FCSTD DOCUMENT  (FreeCAD 0.20R29410 (Git))
Label: FanController
License: All rights reserved
LicenseURL: http://en.wikipedia.org/wiki/All_rights_reserved
objects: PartDesign::Body×2, Sketcher::SketchObject×1
note: 3 computed .brp shape members not serialized (recipe doc carries the construction recipe); baked Part::Feature solids carry a one-line shape summary decoded from their .brp

FEATURE [Sketcher::SketchObject] Sketch  label="bottom001"
  FullyConstrained = true
  MapMode = 5
  Support = -> [XY_Plane]
  sketch-geometry (78):
    g0: LineSegment StartX=-242.5 StartY=-23 StartZ=0 EndX=242.5 EndY=-23 EndZ=0
    g1: LineSegment StartX=242.5 StartY=23 StartZ=0 EndX=-242.5 EndY=23 EndZ=0
    g2: ArcOfCircle CenterX=-215.5 CenterY=16 CenterZ=0 NormalX=0 NormalY=0 NormalZ=1 AngleXU=0 Radius=3 StartAngle=4.71239 EndAngle=7.85398
    g3: LineSegment StartX=-242.5 StartY=19 StartZ=0 EndX=-215.5 EndY=19 EndZ=0
    g4: LineSegment StartX=-215.5 StartY=13 StartZ=0 EndX=-242.5 EndY=13 EndZ=0
    g5: ArcOfCircle CenterX=-215.5 CenterY=-2e-16 CenterZ=0 NormalX=0 NormalY=0 NormalZ=1 AngleXU=0 Radius=3 StartAngle=4.71239 EndAngle=7.85398
    g6: LineSegment StartX=-242.5 StartY=3 StartZ=0 EndX=-215.5 EndY=3 EndZ=0
    g7: LineSegment StartX=-215.5 StartY=-3 StartZ=0 EndX=-242.5 EndY=-3 EndZ=0
    g8: ArcOfCircle CenterX=-215.5 CenterY=-16 CenterZ=0 NormalX=0 NormalY=0 NormalZ=1 AngleXU=0 Radius=3 StartAngle=4.71239 EndAngle=7.85398
    g9: LineSegment StartX=-215.5 StartY=-13 StartZ=0 EndX=-242.5 EndY=-13 EndZ=0
    g10: LineSegment StartX=-215.5 StartY=-19 StartZ=0 EndX=-242.5 EndY=-19 EndZ=0
    g11: ArcOfCircle CenterX=215.5 CenterY=-16 CenterZ=0 NormalX=0 NormalY=0 NormalZ=1 AngleXU=0 Radius=3 StartAngle=1.5708 EndAngle=4.71239
    g12: ArcOfCircle CenterX=215.5 CenterY=2e-16 CenterZ=0 NormalX=0 NormalY=0 NormalZ=1 AngleXU=0 Radius=3 StartAngle=1.5708 EndAngle=4.71239
    g13: ArcOfCircle CenterX=215.5 CenterY=16 CenterZ=0 NormalX=0 NormalY=0 NormalZ=1 AngleXU=0 Radius=3 StartAngle=1.5708 EndAngle=4.71239
    g14: LineSegment StartX=215.5 StartY=19 StartZ=0 EndX=242.5 EndY=19 EndZ=0
    g15: LineSegment StartX=215.5 StartY=13 StartZ=0 EndX=242.5 EndY=13 EndZ=0
    g16: LineSegment StartX=215.5 StartY=3 StartZ=0 EndX=242.5 EndY=3 EndZ=0
    g17: LineSegment StartX=215.5 StartY=-3 StartZ=0 EndX=242.5 EndY=-3 EndZ=0
    g18: LineSegment StartX=215.5 StartY=-13 StartZ=0 EndX=242.5 EndY=-13 EndZ=0
    g19: LineSegment StartX=215.5 StartY=-19 StartZ=0 EndX=242.5 EndY=-19 EndZ=0
    g20: Circle CenterX=-145 CenterY=18 CenterZ=0 NormalX=0 NormalY=0 NormalZ=1 AngleXU=0 Radius=1.6
    g21: GeomPoint X=0 Y=23 Z=0
    g22: Circle CenterX=-145 CenterY=18 CenterZ=0 NormalX=0 NormalY=0 NormalZ=1 AngleXU=0 Radius=3
    g23: Circle CenterX=-145 CenterY=18 CenterZ=0 NormalX=0 NormalY=0 NormalZ=1 AngleXU=0 Radius=3.25
    g24: Circle CenterX=-145 CenterY=-18 CenterZ=0 NormalX=0 NormalY=0 NormalZ=1 AngleXU=0 Radius=1.6
    g25: Circle CenterX=-145 CenterY=-18 CenterZ=0 NormalX=0 NormalY=0 NormalZ=1 AngleXU=0 Radius=3
    g26: Circle CenterX=-145 CenterY=-18 CenterZ=0 NormalX=0 NormalY=0 NormalZ=1 AngleXU=0 Radius=3.25
    g27: Circle CenterX=145 CenterY=-18 CenterZ=0 NormalX=0 NormalY=0 NormalZ=1 AngleXU=0 Radius=1.6
    g28: Circle CenterX=145 CenterY=-18 CenterZ=0 NormalX=0 NormalY=0 NormalZ=1 AngleXU=0 Radius=3
    g29: Circle CenterX=145 CenterY=-18 CenterZ=0 NormalX=0 NormalY=0 NormalZ=1 AngleXU=0 Radius=3.25
    g30: Circle CenterX=145 CenterY=18 CenterZ=0 NormalX=0 NormalY=0 NormalZ=1 AngleXU=0 Radius=3.25
    g31: LineSegment StartX=-242.5 StartY=23 StartZ=0 EndX=-242.5 EndY=19 EndZ=0
    g32: LineSegment StartX=-242.5 StartY=13 StartZ=0 EndX=-242.5 EndY=3 EndZ=0
    g33: LineSegment StartX=-242.5 StartY=-3 StartZ=0 EndX=-242.5 EndY=-13 EndZ=0
    g34: LineSegment StartX=-242.5 StartY=-19 StartZ=0 EndX=-242.5 EndY=-23 EndZ=0
    g35: Circle CenterX=145 CenterY=18 CenterZ=0 NormalX=0 NormalY=0 NormalZ=1 AngleXU=0 Radius=1.6
    g36: Circle CenterX=145 CenterY=18 CenterZ=0 NormalX=0 NormalY=0 NormalZ=1 AngleXU=0 Radius=3
    g37: LineSegment StartX=242.5 StartY=23 StartZ=0 EndX=242.5 EndY=19 EndZ=0
    g38: LineSegment StartX=242.5 StartY=19 StartZ=0 EndX=242.5 EndY=13 EndZ=0
    g39: LineSegment StartX=242.5 StartY=13 StartZ=0 EndX=242.5 EndY=3 EndZ=0
    g40: LineSegment StartX=242.5 StartY=-3 StartZ=0 EndX=242.5 EndY=-13 EndZ=0
    g41: LineSegment StartX=242.5 StartY=-19 StartZ=0 EndX=242.5 EndY=-23 EndZ=0
    g42: Circle CenterX=34.3 CenterY=19.65 CenterZ=0 NormalX=0 NormalY=0 NormalZ=1 AngleXU=0 Radius=1.6
    g43: Circle CenterX=34.3 CenterY=19.65 CenterZ=0 NormalX=0 NormalY=0 NormalZ=1 AngleXU=0 Radius=3
    g44: Circle CenterX=34.3 CenterY=19.65 CenterZ=0 NormalX=0 NormalY=0 NormalZ=1 AngleXU=0 Radius=3.25
    g45: Circle CenterX=34.3 CenterY=-19.65 CenterZ=0 NormalX=0 NormalY=0 NormalZ=1 AngleXU=0 Radius=1.6
    g46: Circle CenterX=34.3 CenterY=-19.65 CenterZ=0 NormalX=0 NormalY=0 NormalZ=1 AngleXU=0 Radius=3
    g47: Circle CenterX=34.3 CenterY=-19.65 CenterZ=0 NormalX=0 NormalY=0 NormalZ=1 AngleXU=0 Radius=3.25
    g48: Circle CenterX=-34.3 CenterY=19.65 CenterZ=0 NormalX=0 NormalY=0 NormalZ=1 AngleXU=0 Radius=1.6
    g49: Circle CenterX=-34.3 CenterY=19.65 CenterZ=0 NormalX=0 NormalY=0 NormalZ=1 AngleXU=0 Radius=3
    g50: Circle CenterX=-34.3 CenterY=19.65 CenterZ=0 NormalX=0 NormalY=0 NormalZ=1 AngleXU=0 Radius=3.25
    g51: Circle CenterX=-34.3 CenterY=-19.65 CenterZ=0 NormalX=0 NormalY=0 NormalZ=1 AngleXU=0 Radius=1.6
    g52: Circle CenterX=-34.3 CenterY=-19.65 CenterZ=0 NormalX=0 NormalY=0 NormalZ=1 AngleXU=0 Radius=3
    g53: Circle CenterX=-34.3 CenterY=-19.65 CenterZ=0 NormalX=0 NormalY=0 NormalZ=1 AngleXU=0 Radius=3.25
    g54: LineSegment StartX=-150.5 StartY=-20.5 StartZ=0 EndX=-150.5 EndY=-18 EndZ=0
    g55: LineSegment StartX=-150.5 StartY=-15.5 StartZ=0 EndX=-150.5 EndY=-13 EndZ=0
    g56: LineSegment StartX=-152.5 StartY=-13 StartZ=0 EndX=-152.5 EndY=-15.5 EndZ=0
    g57: LineSegment StartX=-152.5 StartY=-20.5 StartZ=0 EndX=-152.5 EndY=-18 EndZ=0
    g58: LineSegment StartX=-152.5 StartY=-15.5 StartZ=0 EndX=-150.5 EndY=-15.5 EndZ=0
    g59: LineSegment StartX=-152.5 StartY=-13 StartZ=0 EndX=-150.5 EndY=-13 EndZ=0
    g60: LineSegment StartX=-152.5 StartY=-18 StartZ=0 EndX=-150.5 EndY=-18 EndZ=0
    g61: LineSegment StartX=-150.5 StartY=-20.5 StartZ=0 EndX=-152.5 EndY=-20.5 EndZ=0
    g62: LineSegment StartX=-150.5 StartY=20.5 StartZ=0 EndX=-150.5 EndY=18 EndZ=0
    g63: LineSegment StartX=-150.5 StartY=15.5 StartZ=0 EndX=-150.5 EndY=13 EndZ=0
    g64: LineSegment StartX=-152.5 StartY=20.5 StartZ=0 EndX=-152.5 EndY=18 EndZ=0
    g65: LineSegment StartX=-152.5 StartY=15.5 StartZ=0 EndX=-152.5 EndY=13 EndZ=0
    g66: LineSegment StartX=-152.5 StartY=20.5 StartZ=0 EndX=-150.5 EndY=20.5 EndZ=0
    g67: LineSegment StartX=-150.5 StartY=18 StartZ=0 EndX=-152.5 EndY=18 EndZ=0
    g68: LineSegment StartX=-152.5 StartY=15.5 StartZ=0 EndX=-150.5 EndY=15.5 EndZ=0
    g69: LineSegment StartX=-150.5 StartY=13 StartZ=0 EndX=-152.5 EndY=13 EndZ=0
    g70: LineSegment StartX=150.5 StartY=-15.5 StartZ=0 EndX=150.5 EndY=-20.5 EndZ=0
    g71: LineSegment StartX=152.5 StartY=-20.5 StartZ=0 EndX=152.5 EndY=-15.5 EndZ=0
    g72: LineSegment StartX=150.5 StartY=-20.5 StartZ=0 EndX=152.5 EndY=-20.5 EndZ=0
    g73: LineSegment StartX=152.5 StartY=-15.5 StartZ=0 EndX=150.5 EndY=-15.5 EndZ=0
    g74: LineSegment StartX=150.5 StartY=20.5 StartZ=0 EndX=150.5 EndY=15.5 EndZ=0
    g75: LineSegment StartX=152.5 StartY=20.5 StartZ=0 EndX=152.5 EndY=15.5 EndZ=0
    g76: LineSegment StartX=150.5 StartY=20.5 StartZ=0 EndX=152.5 EndY=20.5 EndZ=0
    g77: LineSegment StartX=150.5 StartY=15.5 StartZ=0 EndX=152.5 EndY=15.5 EndZ=0
  constraints (222):
    c: Horizontal(g0)
    c: Horizontal(g1)
    c: DistanceX(g1,g1) = 485
    c: DistanceY(g0,g1) = 46
    c: Diameter(g2) = 6
    c: Vertical(g2,g2)
    c: Vertical(g2,g2)
    c: Coincident(g3,g2)
    c: Coincident(g4,g2)
    c: Parallel(g3,g1)
    c: Parallel(g1,g4)
    c: Diameter(g5) = 6
    c: Vertical(g5,g5)
    c: Vertical(g5,g5)
    c: Coincident(g6,g5)
    c: Coincident(g7,g5)
    c: Diameter(g8) = 6
    c: Vertical(g8,g8)
    c: Vertical(g8,g8)
    c: Coincident(g9,g8)
    c: Horizontal(g9)
    c: Coincident(g10,g8)
    c: Horizontal(g10)
    c: Parallel(g1,g6)
    c: Parallel(g1,g7)
    c: Equal(g12,g13)
    c: Equal(g12,g11)
    c: Diameter(g12) = 6
    c: Vertical(g13,g13)
    c: Vertical(g13,g13)
    c: Vertical(g12,g12)
    c: Vertical(g12,g12)
    c: Vertical(g11,g11)
    c: Vertical(g11,g11)
    c: Vertical(g13,g12)
    c: Vertical(g12,g11)
    c: Coincident(g14,g13)
    c: Horizontal(g14)
    c: Coincident(g15,g13)
    c: Horizontal(g15)
    c: Coincident(g16,g12)
    c: Horizontal(g16)
    c: Coincident(g17,g12)
    c: Horizontal(g17)
    c: Coincident(g18,g11)
    c: Horizontal(g18)
    c: Coincident(g19,g11)
    c: Horizontal(g19)
    c: DistanceX(g13,g14) = 27
    c: Vertical(g2,g5)
    c: Vertical(g5,g8)
    c: Diameter(g20) = 3.2
    c: PointOnObject(g21,g1)
    c: PointOnObject(g21,g-2)
    c: Coincident(g22,g20)
    c: Diameter(g22) = 6
    c: Coincident(g23,g20)
    c: Diameter(g23) = 6.5
    c: Coincident(g25,g24)
    c: Coincident(g26,g24)
    c: Diameter(g24) = 3.2
    c: Diameter(g25) = 6
    c: Diameter(g26) = 6.5
    c: Coincident(g29,g28)
    c: Coincident(g27,g28)
    c: Diameter(g27) = 3.2
    c: Diameter(g28) = 6
    c: Diameter(g29) = 6.5
    c: Diameter(g30) = 6.5
    c: Vertical(g1,g14)
    c: Vertical(g14,g15)
    c: Vertical(g15,g16)
    c: Vertical(g16,g17)
    c: Vertical(g17,g18)
    c: Vertical(g18,g19)
    c: Vertical(g19,g0)
    c: Vertical(g3,g1)
    c: Vertical(g1,g4)
    c: Vertical(g4,g6)
    c: Vertical(g6,g7)
    c: Vertical(g7,g9)
    c: Vertical(g9,g10)
    c: Vertical(g10,g0)
    c: DistanceY(g-1,g21) = 23
    c: DistanceX(g1,g21) = 242.5
    c: Coincident(g31,g1)
    c: Coincident(g31,g3)
    c: Coincident(g32,g4)
    c: Coincident(g32,g6)
    c: Coincident(g33,g7)
    c: Coincident(g33,g9)
    c: Coincident(g34,g10)
    c: Coincident(g34,g0)
    c: Distance(g3,g1) = 4
    c: Distance(g4,g6) = 10
    c: Distance(g7,g9) = 10
    c: DistanceX(g3,g3) = 27
    c: Coincident(g35,g30)
    c: Coincident(g36,g30)
    c: Diameter(g35) = 3.2
    c: Diameter(g36) = 6
    c: Coincident(g37,g1)
    c: Coincident(g37,g14)
    c: Coincident(g38,g14)
    c: Coincident(g38,g15)
    c: Coincident(g39,g15)
    c: Coincident(g39,g16)
    c: Coincident(g40,g17)
    c: Coincident(g40,g18)
    c: Coincident(g41,g19)
    c: Coincident(g41,g0)
    c: DistanceY(g37,g37) = 4
    c: DistanceY(g39,g39) = 10
    c: DistanceY(g40,g40) = 10
    c: Coincident(g42,g43)
    c: Coincident(g42,g44)
    c: Coincident(g49,g48)
    c: Coincident(g52,g51)
    c: Coincident(g45,g46)
    c: Coincident(g45,g47)
    c: Coincident(g51,g53)
    c: Coincident(g48,g50)
    c: Diameter(g48) = 3.2
    c: Diameter(g49) = 6
    c: Diameter(g50) = 6.5
    c: Diameter(g42) = 3.2
    c: Diameter(g43) = 6
    c: Diameter(g44) = 6.5
    c: Diameter(g51) = 3.2
    c: Diameter(g52) = 6
    c: Diameter(g53) = 6.5
    c: Diameter(g45) = 3.2
    c: Diameter(g46) = 6
    c: Diameter(g47) = 6.5
    c: DistanceY(g-1,g42) = 19.65
    c: DistanceX(g-2,g42) = 34.3
    c: DistanceX(g-2,g45) = 34.3
    c: DistanceY(g-1,g45) = -19.65
    c: DistanceX(g-2,g51) = -34.3
    c: DistanceY(g-1,g51) = -19.65
    c: DistanceX(g-2,g48) = -34.3
    c: Distance(g48,g-1) = 19.65
    c: DistanceX(g-2,g30) = 145
    c: DistanceY(g-1,g30) = 18
    c: DistanceX(g-2,g27) = 145
    c: DistanceY(g-1,g27) = -18
    c: DistanceX(g-2,g20) = -145
    c: DistanceX(g-2,g24) = -145
    c: DistanceY(g-1,g20) = 18
    c: DistanceY(g-1,g24) = -18
    c: Vertical(g54)
    c: DistanceX(g-2,g54) = -150.5
    c: Distance(g54,g0) = 2.5
    c: Distance(g54) = 2.5
    c: Vertical(g55)
    c: Vertical(g54,g55)
    c: Distance(g55,g54) = 2.5
    c: Distance(g55) = 2.5
    c: Vertical(g56)
    c: Vertical(g57)
    c: Coincident(g58,g56)
    c: Coincident(g58,g55)
    c: Horizontal(g58)
    c: Coincident(g59,g56)
    c: Coincident(g59,g55)
    c: Horizontal(g59)
    c: Distance(g59) = 2
    c: Horizontal(g54,g57)
    c: Horizontal(g54,g57)
    c: Coincident(g60,g57)
    c: Coincident(g60,g54)
    c: Coincident(g61,g54)
    c: Coincident(g61,g57)
    c: Distance(g61) = 2
    c: Vertical(g62)
    c: Vertical(g63)
    c: Vertical(g64)
    c: Vertical(g65)
    c: Vertical(g55,g63)
    c: Vertical(g63,g62)
    c: Horizontal(g63,g65)
    c: Horizontal(g63,g65)
    c: Horizontal(g62,g64)
    c: Horizontal(g62,g64)
    c: Distance(g62,g1) = 2.5
    c: Distance(g62) = 2.5
    c: Distance(g62,g63) = 2.5
    c: Distance(g63) = 2.5
    c: Coincident(g66,g64)
    c: Coincident(g66,g62)
    c: Coincident(g67,g62)
    c: Coincident(g67,g64)
    c: Coincident(g68,g65)
    c: Coincident(g68,g63)
    c: Coincident(g69,g63)
    c: Coincident(g69,g65)
    c: Distance(g69) = 2
    c: Distance(g67) = 2
    c: Vertical(g70)
    c: DistanceX(g-2,g70) = 150.5
    c: Distance(g70,g0) = 2.5
    c: Distance(g70) = 5
    c: Vertical(g71)
    c: Horizontal(g70,g71)
    c: Horizontal(g70,g71)
    c: Coincident(g72,g70)
    c: Coincident(g72,g71)
    c: Coincident(g73,g71)
    c: Coincident(g73,g70)
    c: Distance(g73) = 2
    c: Vertical(g74)
    c: Vertical(g74,g70)
    c: Distance(g74) = 5
    c: Distance(g74,g1) = 2.5
    c: Vertical(g75)
    c: Horizontal(g74,g75)
    c: Horizontal(g75,g74)
    c: Coincident(g76,g74)
    c: Coincident(g76,g75)
    c: Coincident(g77,g74)
    c: Coincident(g77,g75)
    c: Distance(g76) = 2
FEATURE [PartDesign::Body] Body  label="bottom"
  Group = -> [Sketch]
  Origin = -> Origin
FEATURE [PartDesign::Body] Body001
  Origin = -> Origin001
